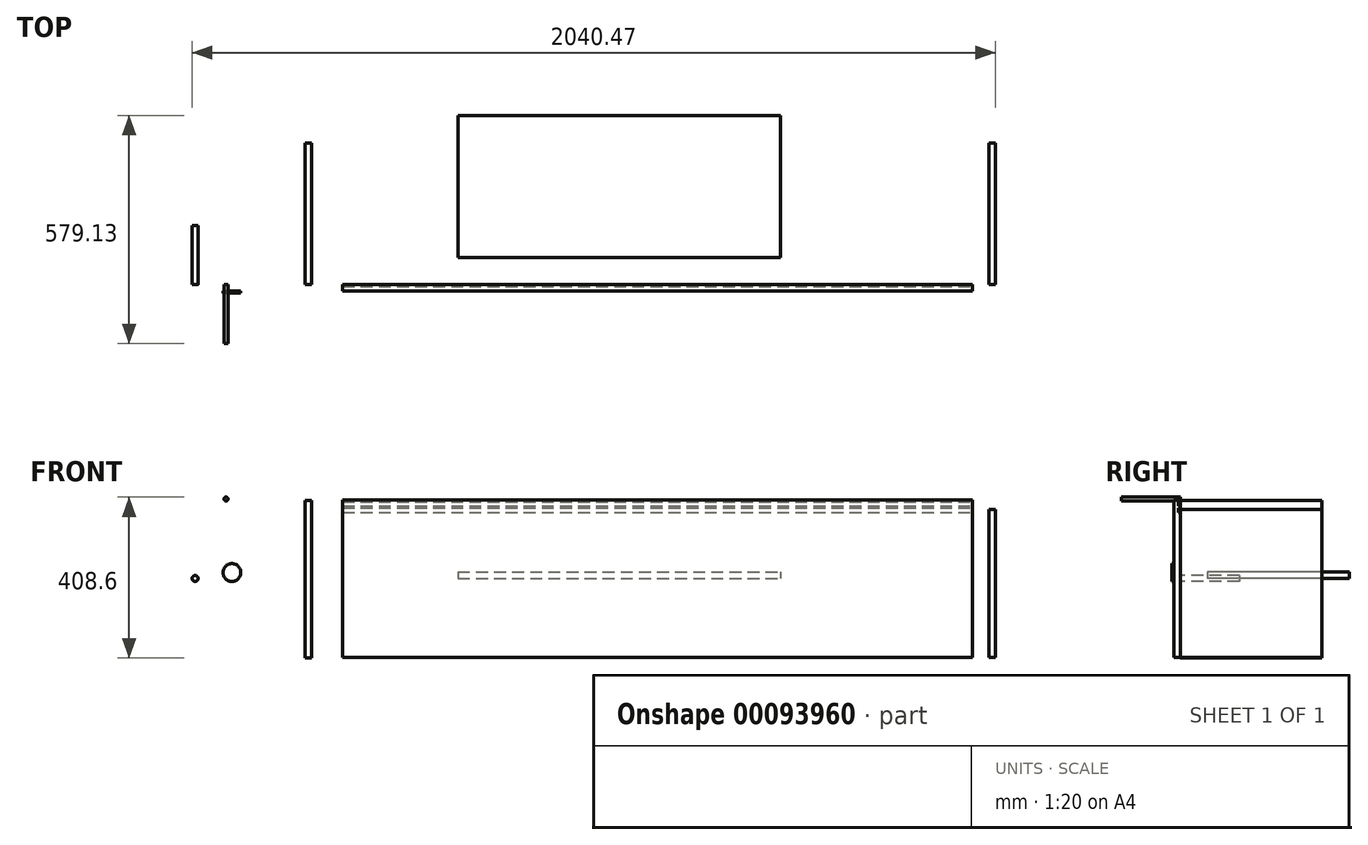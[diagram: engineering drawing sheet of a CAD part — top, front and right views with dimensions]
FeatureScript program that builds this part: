
annotation { "Feature Type Name" : "Feature", "Feature Type Description" : "" }
export const myFeature = defineFeature(function(context is Context, id is Id, definition is map)
    precondition{}
    {
        {
            var Q0;
            Q0=qCreatedBy(makeId("Front.planeOp"),FACE);
            var sketch = newSketch(context, id + "F0", { "sketchPlane" : qUnion([Q0])});
            skLineSegment(sketch, "E0.bottom", {"start": v(800, 200) * mm, "end": v(-800, 200) * mm});
            skLineSegment(sketch, "E0.top", {"start": v(800, -200) * mm, "end": v(-800, -200) * mm});
            skLineSegment(sketch, "E0.left", {"start": v(800, 200) * mm, "end": v(800, -200) * mm});
            skLineSegment(sketch, "E0.right", {"start": v(-800, 200) * mm, "end": v(-800, -200) * mm});
            skPoint(sketch, "E0.middle", {"position": v(0, 0) * mm});
            skSolve(sketch);
        }
        {
            var Q0;
            Q0 = qSketchRegion(id + "F0", true);
            extrude(context, id + "F1", {"entities" : qUnion([Q0]), "depth" : 16 * mm});
        }
        {
            var Q0;
            Q0=makeQuery(id+"F1.opExtrude","CAP_FACE",FACE,{"disambiguationData":[OSD([sQuery(id+"F0.wireOp",EDGE,"E0.bottom"),sQuery(id+"F0.wireOp",EDGE,"E0.top"),sQuery(id+"F0.wireOp",EDGE,"E0.left"),sQuery(id+"F0.wireOp",EDGE,"E0.right")])],"isStart":true});
            var sketch = newSketch(context, id + "F2", { "sketchPlane" : qUnion([Q0])});
            skLineSegment(sketch, "E1.bottom", {"start": v(895.46, 198.23) * mm, "end": v(879.46, 198.23) * mm});
            skLineSegment(sketch, "E1.top", {"start": v(895.46, -201.77) * mm, "end": v(879.46, -201.77) * mm});
            skLineSegment(sketch, "E1.left", {"start": v(895.46, 198.23) * mm, "end": v(895.46, -201.77) * mm});
            skLineSegment(sketch, "E1.right", {"start": v(879.46, 198.23) * mm, "end": v(879.46, -201.77) * mm});
            skLineSegment(sketch, "E2.bottom", {"start": v(8, 200) * mm, "end": v(-8, 200) * mm});
            skLineSegment(sketch, "E2.top", {"start": v(8, -200) * mm, "end": v(-8, -200) * mm});
            skLineSegment(sketch, "E2.left", {"start": v(8, 200) * mm, "end": v(8, -200) * mm});
            skLineSegment(sketch, "E2.right", {"start": v(-8, 200) * mm, "end": v(-8, -200) * mm});
            skSolve(sketch);
        }
        {
            var Q0;
            Q0 = qSketchRegion(id + "F2", true);
            extrude(context, id + "F3", {"entities" : qUnion([Q0]), "depth" : 360 * mm});
        }
        {
            var Q0;
            Q0=makeQuery(id+"F1.opExtrude","CAP_FACE",FACE,{"disambiguationData":[OSD([sQuery(id+"F0.wireOp",EDGE,"E0.bottom"),sQuery(id+"F0.wireOp",EDGE,"E0.top"),sQuery(id+"F0.wireOp",EDGE,"E0.left"),sQuery(id+"F0.wireOp",EDGE,"E0.right")])],"isStart":true});
            var sketch = newSketch(context, id + "F4", { "sketchPlane" : qUnion([Q0])});
            skCircle(sketch, "E3", {"center": v(1174.97, 0) * mm, "radius": 7.5 * mm});
            skSolve(sketch);
        }
        {
            var Q0;
            Q0 = qSketchRegion(id + "F4", true);
            extrude(context, id + "F5", {"entities" : qUnion([Q0]), "depth" : 150 * mm});
        }
        {
            var Q0;
            Q0=makeQuery(id+"F1.opExtrude","CAP_FACE",FACE,{"disambiguationData":[OSD([sQuery(id+"F0.wireOp",EDGE,"E0.bottom"),sQuery(id+"F0.wireOp",EDGE,"E0.top"),sQuery(id+"F0.wireOp",EDGE,"E0.left"),sQuery(id+"F0.wireOp",EDGE,"E0.right")])],"isStart":false});
            var sketch = newSketch(context, id + "F6", { "sketchPlane" : qUnion([Q0])});
            skCircle(sketch, "E4", {"center": v(-1081.63, 15.13) * mm, "radius": 22.6 * mm});
            skSolve(sketch);
        }
        {
            var Q0;
            Q0 = qSketchRegion(id + "F6", true);
            extrude(context, id + "F7", {"entities" : qUnion([Q0]), "depth" : 5 * mm});
        }
        {
            var Q0;
            Q0=qCreatedBy(makeId("Front.planeOp"),FACE);
            var sketch = newSketch(context, id + "F8", { "sketchPlane" : qUnion([Q0])});
            skCircle(sketch, "E5", {"center": v(-1096.55, 201.83) * mm, "radius": 5 * mm});
            skSolve(sketch);
        }
        {
            var Q0;
            Q0 = qSketchRegion(id + "F8", true);
            extrude(context, id + "F9", {"entities" : qUnion([Q0]), "depth" : 150 * mm});
        }
        {
            var Q0;
            Q0=makeQuery(id+"F3.opExtrude","SWEPT_BODY",BODY,{"disambiguationData":[OSD([sQuery(id+"F2.wireOp",EDGE,"E2.bottom"),sQuery(id+"F2.wireOp",EDGE,"E2.top"),sQuery(id+"F2.wireOp",EDGE,"E2.left"),sQuery(id+"F2.wireOp",EDGE,"E2.right")])]});
            var Q1;
            Q1=makeQuery(id+"F3.opExtrude","SWEPT_FACE",FACE,{"disambiguationData":[OSD([sQuery(id+"F2.wireOp",EDGE,"E2.right")])]});
            transform(context, id + "F10", {"entities" : qUnion([Q0]), "transformType" : TransformType.TRANSLATION_DISTANCE, "transformDirection" : qUnion([Q1]), "distance" : 850 * mm, "makeCopy" : false});
        }
        {
            var Q0;
            Q0=makeQuery(id+"F3.opExtrude","SWEPT_FACE",FACE,{"disambiguationData":[OSD([sQuery(id+"F2.wireOp",EDGE,"E2.bottom")])]});
            extrude(context, id + "F11", {"entities" : qUnion([Q0]), "operationType" : NewBodyOperationType.REMOVE, "oppositeDirection" : true, "depth" : 25 * mm});
        }
        {
            var Q0;
            Q0=makeQuery(id+"F1.opExtrude","SWEPT_FACE",FACE,{"disambiguationData":[OSD([sQuery(id+"F0.wireOp",EDGE,"E0.left")])]});
            var sketch = newSketch(context, id + "F12", { "sketchPlane" : qUnion([Q0])});
            skLineSegment(sketch, "E6.bottom", {"start": v(0, 194.27) * mm, "end": v(-5, 194.27) * mm});
            skLineSegment(sketch, "E6.top", {"start": v(0, 184.27) * mm, "end": v(-5, 184.27) * mm});
            skLineSegment(sketch, "E6.left", {"start": v(0, 194.27) * mm, "end": v(0, 184.27) * mm});
            skLineSegment(sketch, "E6.right", {"start": v(-5, 194.27) * mm, "end": v(-5, 184.27) * mm});
            skLineSegment(sketch, "E7.bottom", {"start": v(0, 178.62) * mm, "end": v(-5, 178.62) * mm});
            skLineSegment(sketch, "E7.top", {"start": v(0, 167.45) * mm, "end": v(-5, 167.45) * mm});
            skLineSegment(sketch, "E7.left", {"start": v(0, 178.62) * mm, "end": v(0, 167.45) * mm});
            skLineSegment(sketch, "E7.right", {"start": v(-5, 178.62) * mm, "end": v(-5, 167.45) * mm});
            skSolve(sketch);
        }
        {
            var Q0;
            Q0 = qSketchRegion(id + "F12", true);
            extrude(context, id + "F13", {"entities" : qUnion([Q0]), "operationType" : NewBodyOperationType.REMOVE, "endBound" : BoundingType.THROUGH_ALL, "oppositeDirection" : true, "depth" : 25 * mm});
        }
        {
            var Q0;
            Q0=qCreatedBy(makeId("Top.planeOp"),FACE);
            var sketch = newSketch(context, id + "F14", { "sketchPlane" : qUnion([Q0])});
            skLineSegment(sketch, "E8.bottom", {"start": v(-507.45, 429.13) * mm, "end": v(312.55, 429.13) * mm});
            skLineSegment(sketch, "E8.top", {"start": v(-507.45, 69.13) * mm, "end": v(312.55, 69.13) * mm});
            skLineSegment(sketch, "E8.left", {"start": v(-507.45, 429.13) * mm, "end": v(-507.45, 69.13) * mm});
            skLineSegment(sketch, "E8.right", {"start": v(312.55, 429.13) * mm, "end": v(312.55, 69.13) * mm});
            skSolve(sketch);
        }
        {
            var Q0;
            Q0 = qSketchRegion(id + "F14", true);
            extrude(context, id + "F15", {"entities" : qUnion([Q0]), "operationType" : NewBodyOperationType.ADD, "depth" : 16 * mm});
        }
    });
